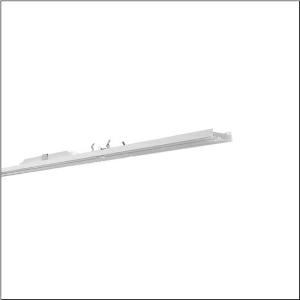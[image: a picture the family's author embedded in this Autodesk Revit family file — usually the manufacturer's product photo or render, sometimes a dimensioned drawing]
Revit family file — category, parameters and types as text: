
# Revit family: licross_r__11_recessed_ho_51ul1edv4m5r_686d
name_source: partatom
category: Lighting Fixtures
units: mm (PartAtom-declared; Revit-internal decimal feet)

## family parameters
Cut with Voids When Loaded = No
Host = Face
Light Source = No
Part Type = Normal
Room Calculation Point = No
Round Connector Dimension = Use Diameter
Shared = No

## types (1)
- --- (1 x LED, 25560 lm, 150.1 W, 4000K)
    Apparent Load = 150 VA
    CIE Flux Codes = 85 95 99 100 100
    Color Rendering = 80
    Color Temperature = 4000K
    Default Elevation = 1800 mm
    Description = Licross® 11 Recessed HO, luminaire insert, of sheet steel, galvanised, coil coated, white, length: 2.250mm, width: 66mm, height: 67mm, LED rated luminous flux: 25.560lm, light colour: 840, control gear: DALI 2, control gear: ECG DALI, with terminal, 5-pole, max. 2.5mm², mains connection: 230V, AC, 50/60Hz, rated input power: 150W, halogen-free wiring, primary optical cover: cover, of PMMA, light emission: direct distribution, primary light characteristic: symmetric, protection rating (complete): IP40, insulation class (complete): insulation class I (protective earthing), certification: CE, ENEC, VDE, UKCA, protection symbol: D if used in an environment without relevant dust loads with corresponding accessories, impact resistance: IK06, permissible ambient temperature for indoor applications: -35..+35°C, corresponds to IFS (International Featured Standards) requirements for safety and quality in the food industry, reducing of maximum allowable ambient temperature of 5°C with ceiling mounting, LABS conformity tested according to VDMA 24364:2018-05, packaging unit: 1 piece
    Height = 58 mm
    Lamp = 1 x LED
    Lamp Light Flux = 25560 lm
    Lamp Power = 150.1 W
    Lamp count = 1
    Length = 2250 mm
    Luminous efficacy = 170 lm/W
    Manufacturer = Siteco
    ModVariant = No
    Model = 51UL1EDV4M5R
    Mounting Place = Ceiling
    Mounting Type = Pendant
    Number of Poles = 1
    OnlyDefault = Yes
    Power Factor = 1
    Product Name = Licross® 11 Recessed HO
    Product group = luminaire insert
    ProductGroupID = 901
    Protection Class = Protection class I
    Protection Degree = IP 40
    RLX_Detail_Level = 1
    RLX_Emergency_Light_Flux = 0 lm
    RLX_Emergency_Type = 0
    RLX_Emergency_Type_DB = No
    RlxData = <blob elided: 26965 chars, md5=2b33cb09>
    Socket = socket
    Standby Power = 0 W
    System Light Flux = 25561 lm
    System Power = 150 W
    Type Comments = factory setting: luminous flux: 100 % | dim-lin: 254 | 575 mA
    Type Image = l_1006953.jpg
    URL = http://relux.com
    VarID = @adj_130679
    Voltage = 0 V
    Weight = 0.00 kg
    Width = 66 mm

## geometry (parser evidence)
native form markers: Blend x4, Sweep x11
no freeform markers — native parametric forms only
